# Revit family: RN 92002 Optifitt-Serra-Raccordo
name_source: partatom
category: Rohrformteile
units: mm (PartAtom-declared; Revit-internal decimal feet)

## family parameters
Arbeitsebenenbasiert = Nein
Beim Laden mit Abzugskörper schneiden = Nein
Bemaßung runder Anschluss = Durchmesser verwenden
Gemeinsam genutzt = Nein
Immer vertikal = Ja
Teiletyp = Verbindung

## types (8) — shared parameters
1.010.00.2 Blattnummer der Richtlinie = 29
1.010.00.3 Ausgabedatum (Monat) der Richtlinie = 201308
1.010.00.4 Herstellername = R. Nussbaum AG
1.010.00.5 Revisionsdatum der Datei = 20190521
1.010.00.6 Webadresse des Herstellers = http://www.nussbaum.ch
1.100.00.4 Produktbezeichnung = Versorgung
1.110.00.2 Index = 3
1.110.00.4 Produktbezeichnung = Optifitt-Serra
1.960/3L.00.8 Link (URL) = https://www.nussbaum.ch
29.700.00.4 Produktname = Optifitt-Serra-Anschlussverschraubung, mit langem Aussengewinde, Gewindeschutz
29.700.00.5 Produktkennung = 2
29.700.00.6 Querschnittsform = 1
29.700.00.7 Nennweitensystem = DN
29.700.00.8 Nenndrucksystem = PN
29.710.02.4 Nenndruck = 16
29.710.02.5 max. zul. Überdruck [hPa] = 1600
29.710.02.7 max. zul. Dauer-Betriebsdruck [hPa] = 1600
29.710.02.9 max. zul. Dauer-Betriebstemperatur [°C] = 90
Connector Visibility = Nein
EnclosingSpace Visibility = Nein
Hersteller = R. Nussbaum AG
URL = https://www.nussbaum.ch

## per-type parameters (varying)
| type | 1.800.00.3 TGA-Nummer | 1.800.00.4 Kommentarfeld | 1.810.00.3 Hersteller-Bestellnummer | 1.810.00.4 DATANORM-Nummer | 1.810.00.6 GTIN-Nummer | 29.710.02.10 Formstück-Gewicht [kg] | 29.710.02.3 Benennung | CONNECTOR0_DIAMETER_dX_0r | CONNECTOR0_dX_01 | CONNECTOR0_ref_dX | CONNECTOR1_DIAMETER_dX_0r | CONNECTOR1_dX_00 | CONNECTOR1_dX_01 | CONNECTOR1_ref_dX | Modell | R. Nussbaum AG 92002.24 de Visibility | R. Nussbaum AG 92002.25 de Visibility | R. Nussbaum AG 92002.26 de Visibility | R. Nussbaum AG 92002.27 de Visibility | R. Nussbaum AG 92002.28 de Visibility | R. Nussbaum AG 92002.29 de Visibility | R. Nussbaum AG 92002.30 de Visibility | R. Nussbaum AG 92002.31 de Visibility | Typenkommentare |
| DN=65 | 01900300000000000000000000000000000000000000000038000000000000000008 | 92002.30, Optifitt-Serra-Anschlussverschraubung, mit langem Aussengewinde, Gewindeschutz, DN=65, L=155 | 92002.3 | 92002.3 | 7612945037015 | 1.818 | Optifitt-Serra-Anschlussverschraubung, mit langem Aussengewinde, Gewindeschutz, DN=65, L=155 | 65 mm | 27 mm | 27 mm | 80 mm | 152 mm | 172 mm | 152 mm | 92002.3 | Nein | Nein | Nein | Nein | Nein | Nein | Ja | Nein | Optifitt-Serra-Raccordo  DN=65 |
| DN=50 | 01900300000000000000000000000000000000000000000038000000000000000007 | 92002.31, Optifitt-Serra-Anschlussverschraubung, mit langem Aussengewinde, Gewindeschutz, DN=50, L=138 | 92002.31 | 92002.31 | 7612945037022 | 1.19 | Optifitt-Serra-Anschlussverschraubung, mit langem Aussengewinde, Gewindeschutz, DN=50, L=138 | 50 mm | 24 mm | 24 mm | 65 mm | 137 mm | 152 mm | 137 mm | 92002.31 | Nein | Nein | Nein | Nein | Nein | Nein | Nein | Ja | Optifitt-Serra-Raccordo  DN=50 |
| DN=50x65 | 01900300000000000000000000000000000000000000000038000000000000000006 | 92002.29, Optifitt-Serra-Anschlussverschraubung, mit langem Aussengewinde, Gewindeschutz, DN=50x65, L=122 | 92002.29 | 92002.29 | 7612945037008 | 1.124 | Optifitt-Serra-Anschlussverschraubung, mit langem Aussengewinde, Gewindeschutz, DN=50x65, L=122 | 50 mm | 24 mm | 24 mm | 65 mm | 122 mm | 137 mm | 122 mm | 92002.29 | Nein | Nein | Nein | Nein | Nein | Ja | Nein | Nein | Optifitt-Serra-Raccordo  DN=50x65 |
| DN=40 | 01900300000000000000000000000000000000000000000038000000000000000005 | 92002.28, Optifitt-Serra-Anschlussverschraubung, mit langem Aussengewinde, Gewindeschutz, DN=40, L=175 | 92002.28 | 92002.28 | 7612945036995 | 1.029 | Optifitt-Serra-Anschlussverschraubung, mit langem Aussengewinde, Gewindeschutz, DN=40, L=175 | 40 mm | 19 mm | 19 mm | 40 mm | 174 mm | 187 mm | 174 mm | 92002.28 | Nein | Nein | Nein | Nein | Ja | Nein | Nein | Nein | Optifitt-Serra-Raccordo  DN=40 |
| DN=32 | 01900300000000000000000000000000000000000000000038000000000000000004 | 92002.27, Optifitt-Serra-Anschlussverschraubung, mit langem Aussengewinde, Gewindeschutz, DN=32, L=165 | 92002.27 | 92002.27 | 7612945036988 | 0.765 | Optifitt-Serra-Anschlussverschraubung, mit langem Aussengewinde, Gewindeschutz, DN=32, L=165 | 32 mm | 19 mm | 19 mm | 40 mm | 164 mm  [stored 0.538058 ft] | 176 mm | 164 mm  [stored 0.538058 ft] | 92002.27 | Nein | Nein | Nein | Ja | Nein | Nein | Nein | Nein | Optifitt-Serra-Raccordo  DN=32 |
| DN=25 | 01900300000000000000000000000000000000000000000038000000000000000003 | 92002.26, Optifitt-Serra-Anschlussverschraubung, mit langem Aussengewinde, Gewindeschutz, DN=25, L=138 | 92002.26 | 92002.26 | 7612945036971 | 0.479 | Optifitt-Serra-Anschlussverschraubung, mit langem Aussengewinde, Gewindeschutz, DN=25, L=138 | 25 mm  [stored 0.082021 ft] | 17 mm | 17 mm | 32 mm | 138 mm | 148 mm | 138 mm | 92002.26 | Nein | Nein | Ja | Nein | Nein | Nein | Nein | Nein | Optifitt-Serra-Raccordo  DN=25 |
| DN=20 | 01900300000000000000000000000000000000000000000038000000000000000002 | 92002.25, Optifitt-Serra-Anschlussverschraubung, mit langem Aussengewinde, Gewindeschutz, DN=20, L=121 | 92002.25 | 92002.25 | 7612945036964 | 0.282 | Optifitt-Serra-Anschlussverschraubung, mit langem Aussengewinde, Gewindeschutz, DN=20, L=121 | 20 mm | 15 mm  [stored 0.0492126 ft] | 15 mm  [stored 0.0492126 ft] | 25 mm  [stored 0.082021 ft] | 122 mm | 130 mm | 122 mm | 92002.25 | Nein | Ja | Nein | Nein | Nein | Nein | Nein | Nein | Optifitt-Serra-Raccordo  DN=20 |
| DN=15 | 01900300000000000000000000000000000000000000000038000000000000000001 | 92002.24, Optifitt-Serra-Anschlussverschraubung, mit langem Aussengewinde, Gewindeschutz, DN=15, L=108 | 92002.24 | 92002.24 | 7612945036957 | 0.179 | Optifitt-Serra-Anschlussverschraubung, mit langem Aussengewinde, Gewindeschutz, DN=15, L=108 | 15 mm  [stored 0.0492126 ft] | 13 mm | 13 mm | 20 mm | 108 mm  [stored 0.354331 ft] | 116 mm  [stored 0.380577 ft] | 108 mm  [stored 0.354331 ft] | 92002.24 | Ja | Nein | Nein | Nein | Nein | Nein | Nein | Nein | Optifitt-Serra-Raccordo  DN=15 |

note: [stored X ft] marks values corroborated as IEEE doubles in the binary element streams (Revit-internal decimal feet)

## geometry (parser evidence)
native form markers: Sweep x2
no freeform markers — native parametric forms only
